# Revit family: KingswayGroup_PllHndls_ClassicGripAnti-LigaturePullHandleBoltFixed
name_source: partatom
category: Specialty Equipment
units: mm (PartAtom-declared; Revit-internal decimal feet)

## family parameters
Always vertical = Yes
Cut with Voids When Loaded = No
Part Type = Normal
Room Calculation Point = No
Round Connector Dimension = Use Diameter
Shared = No
Work Plane-Based = No

## types (1)
- KingswayGroup_PllHndls_ClassicGripAnti-LigaturePullHandleBoltFixed
    AssetType = Fixed
    BIMObjectName = KingswayGroup_PullHandles_ClassicGripAnti-LigaturePullHandleBoltFixed
    Category = Pr_30_36_59_64:Pull handles
    Color = For full range of available finishes and colours, contact Kingsway Group
    Default Elevation = 0 mm  [stored 0 ft]
    Description = Classic Grip Pull Handle Bolt Fixed
    DurationUnit = year
    Features = The Classic Grip handle is shaped to resist ligature attachment and designed for good grip and improved infection control. The KG61 is a bolt fixed anti-ligature handle that is either used with a KG60 (back plate version) on the other side of the door, or on cupboard or riser doors.
    Finish = For full range of available finishes and colours, contact Kingsway Group
    IfcExportAs = IfcDiscreteAccessoryType
    IfcExportType = USERDEFINED
    Manufacturer = Kingsway Group
    ManufacturerName = Kingsway Group
    ManufacturerURL = https://kingswaygroupglobal.com
    Material = For full range of available material, contact Kingsway Group
    Model = KG61
    ModelNumber = KG61
    ModelReference = Classic Grip Anti-Ligature PullHandle (Bolt Fixed)
    Name = PullHandles_ClassicGripAnti-LigaturePullHandleBoltFixed_KG61_KingswayGroup
    NominalHeight = 199.7 mm  [stored 0.655184 ft]
    NominalLength = 37.5 mm
    NominalWidth = 44.8 mm  [stored 0.146982 ft]
    ProductInformation = https://kingswaygroupglobal.com
    Size = 37.5 x 199.7 x 44.8 mm
    URL = https://kingswaygroupglobal.com
    Uniclass2015Code = Pr_30_36_59_64
    Uniclass2015Title = Pull handles
    Uniclass2015Version = Products v1.36
    Version = 1
    WarrantyDescription = 5-Year Guarantee *For faulty manufacture and not for damage
    WarrantyDurationParts = 5
    WarrantyDurationUnit = year

note: [stored X ft] marks values corroborated as IEEE doubles in the binary element streams (Revit-internal decimal feet)

## geometry (parser evidence)
native form markers: Sweep x3
no freeform markers — native parametric forms only
